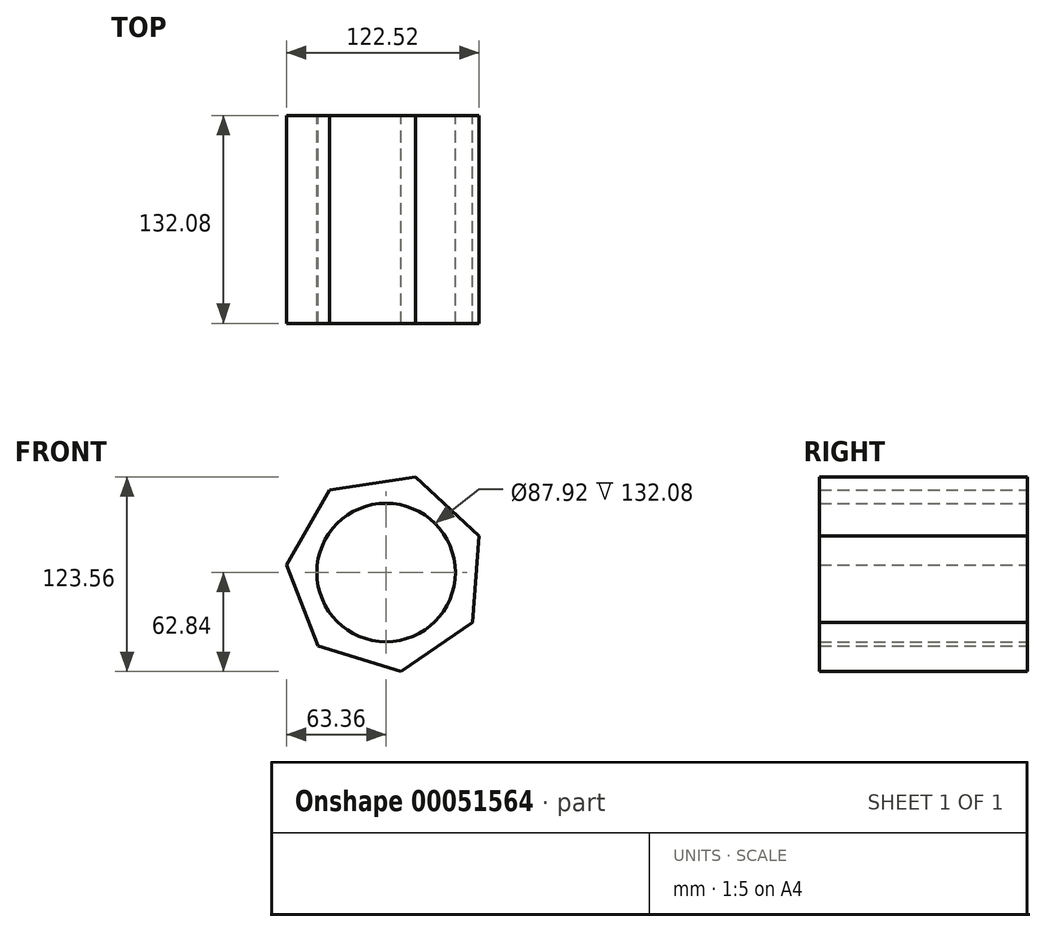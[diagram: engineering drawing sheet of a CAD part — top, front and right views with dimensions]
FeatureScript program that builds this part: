
annotation { "Feature Type Name" : "Feature", "Feature Type Description" : "" }
export const myFeature = defineFeature(function(context is Context, id is Id, definition is map)
    precondition{}
    {
        {
            var Q0;
            Q0=qCreatedBy(makeId("Front.planeOp"),FACE);
            var sketch = newSketch(context, id + "F0", { "sketchPlane" : qUnion([Q0])});
            skCircle(sketch, "E0", {"center": v(0, 0) * mm, "radius": 43.96 * mm});
            skCircle(sketch, "E1.cCircle", {"center": v(0, 0) * mm, "radius": 63.54 * mm, "construction": true});
            skLineSegment(sketch, "E1.0", {"start": v(-63.36, 4.76) * mm, "end": v(-35.79, 52.5) * mm});
            skLineSegment(sketch, "E1.1", {"start": v(-35.79, 52.5) * mm, "end": v(18.74, 60.72) * mm});
            skLineSegment(sketch, "E1.2", {"start": v(18.74, 60.72) * mm, "end": v(59.16, 23.2) * mm});
            skLineSegment(sketch, "E1.3", {"start": v(59.16, 23.2) * mm, "end": v(55.02, -31.78) * mm});
            skLineSegment(sketch, "E1.4", {"start": v(55.02, -31.78) * mm, "end": v(9.46, -62.84) * mm});
            skLineSegment(sketch, "E1.5", {"start": v(9.46, -62.84) * mm, "end": v(-43.23, -46.57) * mm});
            skLineSegment(sketch, "E1.6", {"start": v(-43.23, -46.57) * mm, "end": v(-63.36, 4.76) * mm});
            skSolve(sketch);
        }
        {
            var Q0;
            Q0 = qSketchRegion(id + "F0", true);
            extrude(context, id + "F1", {"entities" : qUnion([Q0]), "depth" : 132.08 * mm});
        }
    });
